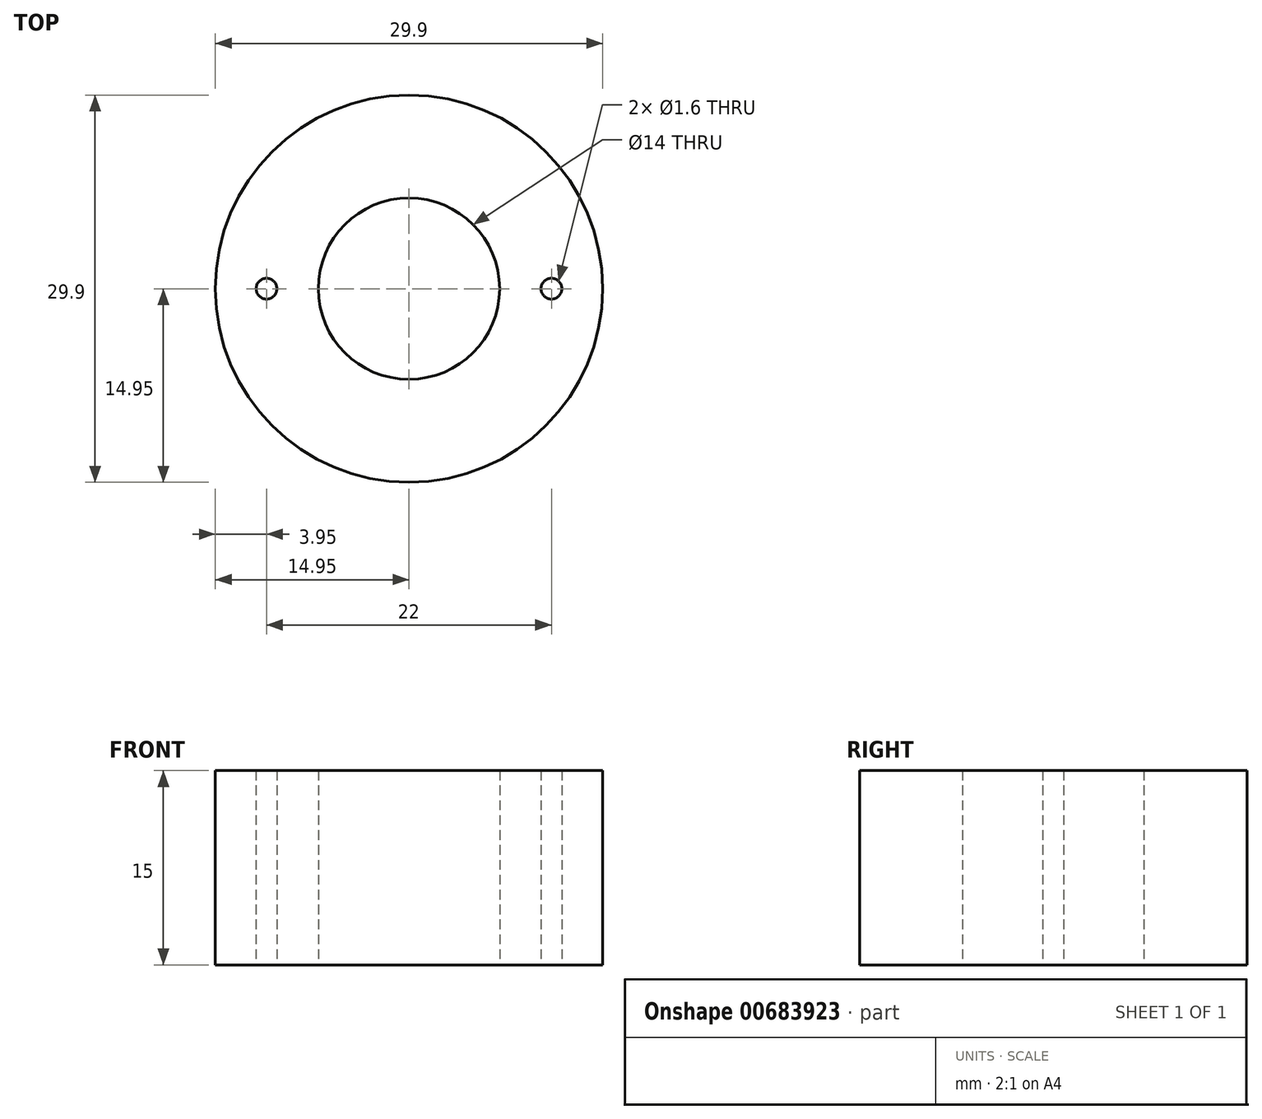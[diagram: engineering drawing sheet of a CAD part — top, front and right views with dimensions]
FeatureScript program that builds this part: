
annotation { "Feature Type Name" : "Feature", "Feature Type Description" : "" }
export const myFeature = defineFeature(function(context is Context, id is Id, definition is map)
    precondition{}
    {
        {
            var Q0;
            Q0=qCreatedBy(makeId("Top.planeOp"),FACE);
            var sketch = newSketch(context, id + "F0", { "sketchPlane" : qUnion([Q0])});
            skCircle(sketch, "E0", {"center": v(0, 0) * mm, "radius": 14.95 * mm});
            skSolve(sketch);
        }
        {
            var Q0;
            Q0=makeQuery(id+"F0.imprint","IMPRINT",FACE,{"disambiguationData":[TD([[makeQuery(id+"F0.imprint","IMPRINT",EDGE,{"derivedFrom":sQuery(id+"F0.wireOp",EDGE,"E0")}),1.0]])]});
            var Q1;
            Q1=sQuery(id+"F0.wireOp",EDGE,"E0");
            extrude(context, id + "F1", {"entities" : qUnion([Q0]), "surfaceEntities" : qUnion([Q1]), "depth" : 15 * mm, "offsetDistance" : 25 * mm});
        }
        {
            var Q0;
            Q0=qCreatedBy(makeId("Top.planeOp"),FACE);
            var sketch = newSketch(context, id + "F2", { "sketchPlane" : qUnion([Q0])});
            skCircle(sketch, "E1", {"center": v(0, 0) * mm, "radius": 7 * mm});
            skSolve(sketch);
        }
        {
            var Q0;
            Q0=makeQuery(id+"F2.imprint","IMPRINT",FACE,{"disambiguationData":[TD([[makeQuery(id+"F2.imprint","IMPRINT",EDGE,{"derivedFrom":sQuery(id+"F2.wireOp",EDGE,"E1")}),1.0]])]});
            extrude(context, id + "F3", {"entities" : qUnion([Q0]), "operationType" : NewBodyOperationType.REMOVE, "depth" : 15 * mm, "offsetDistance" : 25 * mm});
        }
        {
            var Q0;
            Q0=qCreatedBy(makeId("Top.planeOp"),FACE);
            var sketch = newSketch(context, id + "F4", { "sketchPlane" : qUnion([Q0])});
            skCircle(sketch, "E2", {"center": v(-11, 0) * mm, "radius": 0.8 * mm});
            skCircle(sketch, "E3", {"center": v(11, 0) * mm, "radius": 0.8 * mm});
            skSolve(sketch);
        }
        {
            var Q0;
            Q0 = qSketchRegion(id + "F4", true);
            extrude(context, id + "F5", {"entities" : qUnion([Q0]), "operationType" : NewBodyOperationType.REMOVE, "depth" : 15 * mm, "offsetDistance" : 25 * mm});
        }
    });
